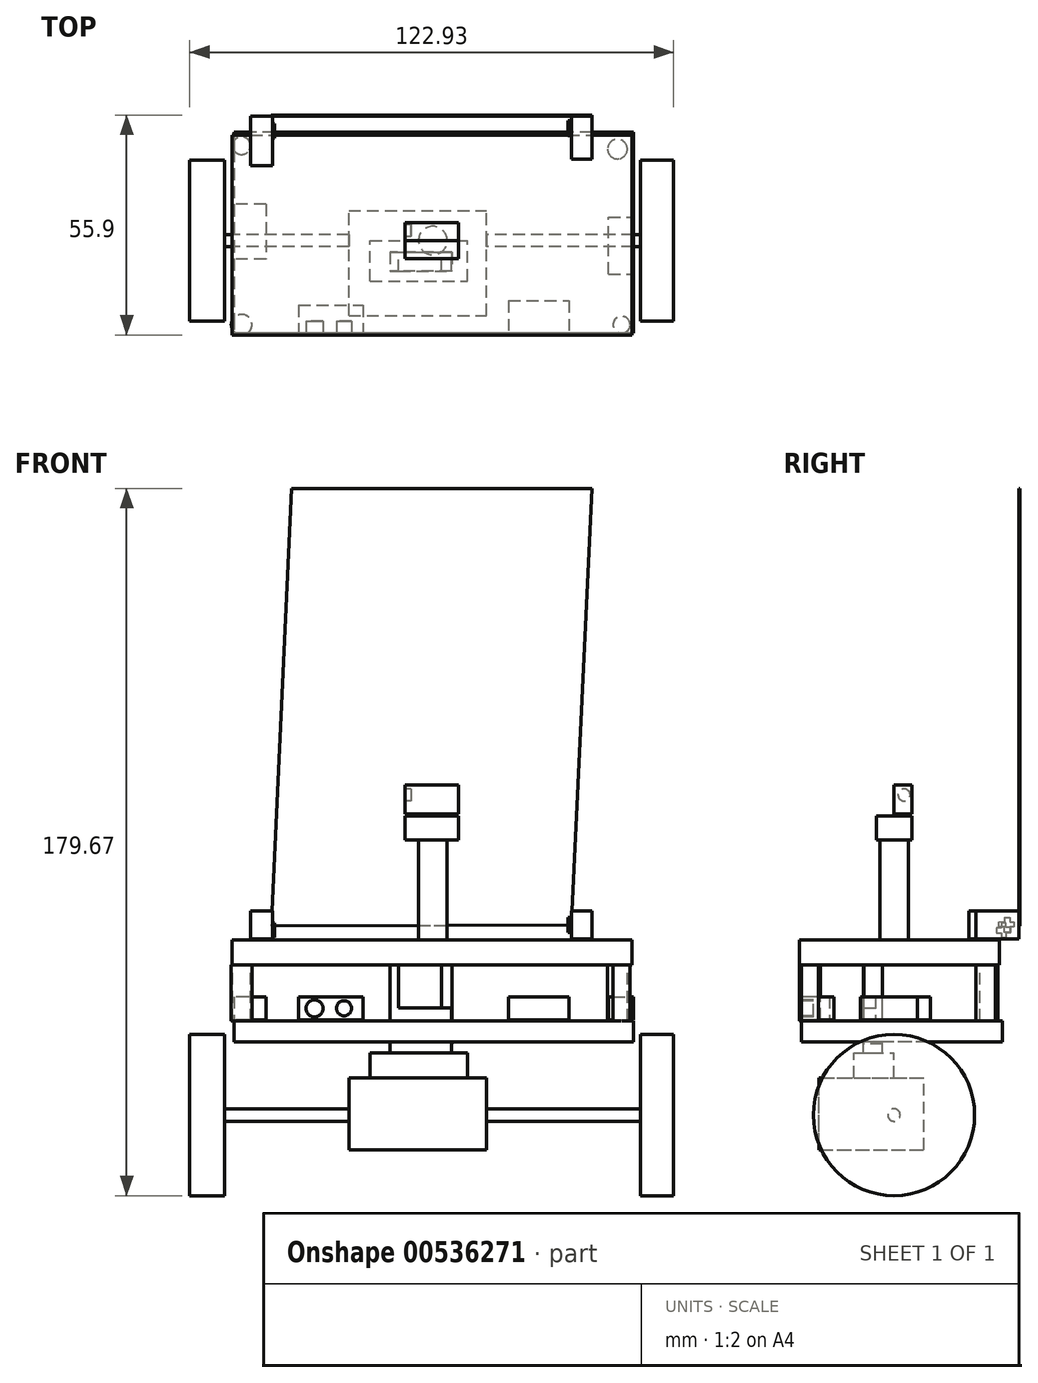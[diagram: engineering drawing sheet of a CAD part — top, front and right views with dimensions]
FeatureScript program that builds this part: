
annotation { "Feature Type Name" : "Feature", "Feature Type Description" : "" }
export const myFeature = defineFeature(function(context is Context, id is Id, definition is map)
    precondition{}
    {
        {
            var Q0;
            Q0=qCreatedBy(makeId("Top.planeOp"),FACE);
            var sketch = newSketch(context, id + "F0", { "sketchPlane" : qUnion([Q0])});
            skLineSegment(sketch, "E0.bottom", {"start": v(-50.99, 26.82) * mm, "end": v(50.61, 26.82) * mm});
            skLineSegment(sketch, "E0.top", {"start": v(-50.99, -23.98) * mm, "end": v(50.61, -23.98) * mm});
            skLineSegment(sketch, "E0.left", {"start": v(-50.99, 26.82) * mm, "end": v(-50.99, -23.98) * mm});
            skLineSegment(sketch, "E0.right", {"start": v(50.61, 26.82) * mm, "end": v(50.61, -23.98) * mm});
            skSolve(sketch);
        }
        {
            var Q0;
            Q0=makeQuery(id+"F0.imprint","IMPRINT",FACE,{"disambiguationData":[TD([[makeQuery(id+"F0.imprint","IMPRINT",EDGE,{"derivedFrom":sQuery(id+"F0.wireOp",EDGE,"E0.bottom")}),-1.0]])]});
            extrude(context, id + "F1", {"entities" : qUnion([Q0]), "depth" : 6.35 * mm, "offsetDistance" : 25.4 * mm});
        }
        {
            var Q0;
            Q0=makeQuery(id+"F1.opExtrude","CAP_FACE",FACE,{"disambiguationData":[OSD([sQuery(id+"F0.wireOp",EDGE,"E0.bottom"),sQuery(id+"F0.wireOp",EDGE,"E0.top"),sQuery(id+"F0.wireOp",EDGE,"E0.left"),sQuery(id+"F0.wireOp",EDGE,"E0.right")])],"isStart":false});
            var sketch = newSketch(context, id + "F2", { "sketchPlane" : qUnion([Q0])});
            skCircle(sketch, "E1", {"center": v(0, 0) * mm, "radius": 3.64 * mm});
            skSolve(sketch);
        }
        {
            var Q0;
            Q0 = qSketchRegion(id + "F2", true);
            extrude(context, id + "F3", {"entities" : qUnion([Q0]), "operationType" : NewBodyOperationType.ADD, "depth" : 25.4 * mm, "offsetDistance" : 25.4 * mm, "hasSecondDirection" : true, "secondDirectionOppositeDirection" : true, "secondDirectionDepth" : 1.02 * mm});
        }
        {
            var Q0;
            Q0=makeQuery(id+"F3.opExtrude","CAP_FACE",FACE,{"disambiguationData":[OSD([sQuery(id+"F2.wireOp",EDGE,"E1")])],"isStart":false});
            var sketch = newSketch(context, id + "F4", { "sketchPlane" : qUnion([Q0])});
            skLineSegment(sketch, "E2.bottom", {"start": v(6.54, -4.52) * mm, "end": v(-7.02, -4.52) * mm});
            skLineSegment(sketch, "E2.top", {"start": v(6.54, 4.54) * mm, "end": v(-7.02, 4.54) * mm});
            skLineSegment(sketch, "E2.left", {"start": v(6.54, -4.52) * mm, "end": v(6.54, 4.54) * mm});
            skLineSegment(sketch, "E2.right", {"start": v(-7.02, -4.52) * mm, "end": v(-7.02, 4.54) * mm});
            skSolve(sketch);
        }
        {
            var Q0;
            Q0 = qSketchRegion(id + "F4", true);
            extrude(context, id + "F5", {"entities" : qUnion([Q0]), "operationType" : NewBodyOperationType.ADD, "depth" : 6.1 * mm, "offsetDistance" : 25.4 * mm});
        }
        {
            var Q0;
            Q0=makeQuery(id+"F5.opExtrude","CAP_FACE",FACE,{"disambiguationData":[OSD([sQuery(id+"F4.wireOp",EDGE,"E2.bottom"),sQuery(id+"F4.wireOp",EDGE,"E2.top"),sQuery(id+"F4.wireOp",EDGE,"E2.left"),sQuery(id+"F4.wireOp",EDGE,"E2.right")])],"isStart":false});
            var sketch = newSketch(context, id + "F6", { "sketchPlane" : qUnion([Q0])});
            skLineSegment(sketch, "E3.bottom", {"start": v(6.54, 0) * mm, "end": v(-7.02, 0) * mm});
            skLineSegment(sketch, "E3.top", {"start": v(6.54, 4.54) * mm, "end": v(-7.02, 4.54) * mm});
            skLineSegment(sketch, "E3.left", {"start": v(6.54, 0) * mm, "end": v(6.54, 4.54) * mm});
            skLineSegment(sketch, "E3.right", {"start": v(-7.02, 0) * mm, "end": v(-7.02, 4.54) * mm});
            skSolve(sketch);
        }
        {
            var Q0;
            Q0 = qSketchRegion(id + "F6", true);
            extrude(context, id + "F7", {"entities" : qUnion([Q0]), "operationType" : NewBodyOperationType.ADD, "depth" : 7.87 * mm, "offsetDistance" : 25.4 * mm, "hasSecondDirection" : true, "secondDirectionOppositeDirection" : false, "secondDirectionDepth" : 0.5 * mm});
        }
        {
            var Q0;
            Q0=makeQuery(id+"F7.boolean.opBoolean","MERGE",FACE,{"derivedFrom":[makeQuery(id+"F5.opExtrude","SWEPT_FACE",FACE,{"disambiguationData":[OSD([sQuery(id+"F4.wireOp",EDGE,"E2.right")])]}),makeQuery(id+"F7.opExtrude","SWEPT_FACE",FACE,{"disambiguationData":[OSD([sQuery(id+"F6.wireOp",EDGE,"tPaWNqs1-bpPp-KasF-azJ7-oUnZ8tWQEHvT.right")])]})]});
            var sketch = newSketch(context, id + "F8", { "sketchPlane" : qUnion([Q0])});
            skCircle(sketch, "E4", {"center": v(-2.58, 43.15) * mm, "radius": 1.54 * mm});
            skCircle(sketch, "E5", {"center": v(2.34, 42.9) * mm, "radius": 1.59 * mm});
            skSolve(sketch);
        }
        {
            var Q0;
            Q0 = qSketchRegion(id + "F8", true);
            extrude(context, id + "F9", {"entities" : qUnion([Q0]), "operationType" : NewBodyOperationType.REMOVE, "oppositeDirection" : true, "depth" : 1.52 * mm, "offsetDistance" : 25.4 * mm});
        }
        {
            var Q0;
            Q0=makeQuery(id+"F1.opExtrude","CAP_FACE",FACE,{"disambiguationData":[OSD([sQuery(id+"F0.wireOp",EDGE,"E0.bottom"),sQuery(id+"F0.wireOp",EDGE,"E0.top"),sQuery(id+"F0.wireOp",EDGE,"E0.left"),sQuery(id+"F0.wireOp",EDGE,"E0.right")])],"isStart":true});
            var sketch = newSketch(context, id + "F10", { "sketchPlane" : qUnion([Q0])});
            skCircle(sketch, "E6", {"center": v(-48.59, 21.36) * mm, "radius": 2.62 * mm});
            skCircle(sketch, "E7", {"center": v(-48.59, -24.13) * mm, "radius": 2.25 * mm});
            skCircle(sketch, "E8", {"center": v(47.96, 21.36) * mm, "radius": 2.16 * mm});
            skCircle(sketch, "E9", {"center": v(46.9, -23.26) * mm, "radius": 2.5 * mm});
            skSolve(sketch);
        }
        {
            var Q0;
            Q0 = qSketchRegion(id + "F10", true);
            extrude(context, id + "F11", {"entities" : qUnion([Q0]), "operationType" : NewBodyOperationType.ADD, "depth" : 14.22 * mm, "offsetDistance" : 25.4 * mm});
        }
        {
            var Q0;
            Q0=makeQuery(id+"F11.opExtrude","CAP_FACE",FACE,{"disambiguationData":[OSD([sQuery(id+"F10.wireOp",EDGE,"E9")])],"isStart":false});
            var sketch = newSketch(context, id + "F12", { "sketchPlane" : qUnion([Q0])});
            skLineSegment(sketch, "E10.bottom", {"start": v(50.97, -27.6) * mm, "end": v(-50.5, -27.6) * mm});
            skLineSegment(sketch, "E10.top", {"start": v(50.97, 23.52) * mm, "end": v(-50.5, 23.52) * mm});
            skLineSegment(sketch, "E10.left", {"start": v(50.97, -27.6) * mm, "end": v(50.97, 23.52) * mm});
            skLineSegment(sketch, "E10.right", {"start": v(-50.5, -27.6) * mm, "end": v(-50.5, 23.52) * mm});
            skSolve(sketch);
        }
        {
            var Q0;
            Q0 = qSketchRegion(id + "F12", true);
            extrude(context, id + "F13", {"entities" : qUnion([Q0]), "operationType" : NewBodyOperationType.ADD, "depth" : 5.33 * mm, "offsetDistance" : 25.4 * mm});
        }
        {
            var Q0;
            {var subQ0=sQuery(id+"F12.wireOp",EDGE,"E10.left");var subQ1=sQuery(id+"F12.wireOp",EDGE,"E10.top");var subQ2=sQuery(id+"F10.wireOp",EDGE,"E8");var subQ3=sQuery(id+"F10.wireOp",EDGE,"E6");var subQ4=sQuery(id+"F12.wireOp",EDGE,"E10.bottom");var subQ5=sQuery(id+"F10.wireOp",EDGE,"E7");var subQ6=sQuery(id+"F12.wireOp",EDGE,"E10.right");Q0=makeQuery(id+"F13.boolean.opBoolean","SPLIT",FACE,{"disambiguationData":[TD([makeQuery(id+"F11.opExtrude","SWEPT_FACE",FACE,{"disambiguationData":[OSD([subQ3])]}),makeQuery(id+"F11.opExtrude","CAP_FACE",FACE,{"disambiguationData":[OSD([subQ3])],"isStart":false}),makeQuery(id+"F11.opExtrude","SWEPT_FACE",FACE,{"disambiguationData":[OSD([subQ5])]}),makeQuery(id+"F11.opExtrude","CAP_FACE",FACE,{"disambiguationData":[OSD([subQ5])],"isStart":false}),makeQuery(id+"F11.opExtrude","SWEPT_FACE",FACE,{"disambiguationData":[OSD([subQ2])]}),makeQuery(id+"F11.opExtrude","CAP_FACE",FACE,{"disambiguationData":[OSD([subQ2])],"isStart":false}),makeQuery(id+"F11.opExtrude","SWEPT_FACE",FACE,{"disambiguationData":[OSD([sQuery(id+"F10.wireOp",EDGE,"E9")])]}),makeQuery(id+"F13.opExtrude","SWEPT_FACE",FACE,{"disambiguationData":[OSD([subQ4])]}),makeQuery(id+"F13.opExtrude","SWEPT_FACE",FACE,{"disambiguationData":[OSD([subQ1])]}),makeQuery(id+"F13.opExtrude","SWEPT_FACE",FACE,{"disambiguationData":[OSD([subQ0])]}),makeQuery(id+"F13.opExtrude","SWEPT_FACE",FACE,{"disambiguationData":[OSD([subQ6])]})])],"derivedFrom":makeQuery(id+"F13.opExtrude","CAP_FACE",FACE,{"disambiguationData":[OSD([subQ4,subQ1,subQ0,subQ6])],"isStart":true})});}
            var sketch = newSketch(context, id + "F14", { "sketchPlane" : qUnion([Q0])});
            skLineSegment(sketch, "E11.bottom", {"start": v(-42.43, 9.27) * mm, "end": v(-50.5, 9.27) * mm});
            skLineSegment(sketch, "E11.top", {"start": v(-42.43, -4.68) * mm, "end": v(-50.5, -4.68) * mm});
            skLineSegment(sketch, "E11.left", {"start": v(-42.43, 9.27) * mm, "end": v(-42.43, -4.68) * mm});
            skLineSegment(sketch, "E11.right", {"start": v(-50.5, 9.27) * mm, "end": v(-50.5, -4.68) * mm});
            skLineSegment(sketch, "E12.bottom", {"start": v(44.61, -8.52) * mm, "end": v(50.97, -8.52) * mm});
            skLineSegment(sketch, "E12.top", {"start": v(44.61, 5.95) * mm, "end": v(50.97, 5.95) * mm});
            skLineSegment(sketch, "E12.left", {"start": v(44.61, -8.52) * mm, "end": v(44.61, 5.95) * mm});
            skLineSegment(sketch, "E12.right", {"start": v(50.97, -8.52) * mm, "end": v(50.97, 5.95) * mm});
            skLineSegment(sketch, "E13.bottom", {"start": v(-34.12, -16.4) * mm, "end": v(-17.71, -16.4) * mm});
            skLineSegment(sketch, "E13.top", {"start": v(-34.12, -23.52) * mm, "end": v(-17.71, -23.52) * mm});
            skLineSegment(sketch, "E13.left", {"start": v(-34.12, -16.4) * mm, "end": v(-34.12, -23.52) * mm});
            skLineSegment(sketch, "E13.right", {"start": v(-17.71, -16.4) * mm, "end": v(-17.71, -23.52) * mm});
            skLineSegment(sketch, "E14.bottom", {"start": v(19.22, -15.3) * mm, "end": v(34.55, -15.3) * mm});
            skLineSegment(sketch, "E14.top", {"start": v(19.22, -23.52) * mm, "end": v(34.55, -23.52) * mm});
            skLineSegment(sketch, "E14.left", {"start": v(19.22, -15.3) * mm, "end": v(19.22, -23.52) * mm});
            skLineSegment(sketch, "E14.right", {"start": v(34.55, -15.3) * mm, "end": v(34.55, -23.52) * mm});
            skSolve(sketch);
        }
        {
            var Q0;
            Q0 = qSketchRegion(id + "F14", true);
            extrude(context, id + "F15", {"entities" : qUnion([Q0]), "operationType" : NewBodyOperationType.ADD, "depth" : 6.1 * mm, "offsetDistance" : 25.4 * mm, "hasSecondDirection" : true, "secondDirectionOppositeDirection" : false, "secondDirectionDepth" : 0.25 * mm});
        }
        {
            var Q0;
            Q0=makeQuery(id+"F15.opExtrude","SWEPT_FACE",FACE,{"disambiguationData":[OSD([sQuery(id+"F14.wireOp",EDGE,"E13.top")])]});
            var sketch = newSketch(context, id + "F16", { "sketchPlane" : qUnion([Q0])});
            skCircle(sketch, "E15", {"center": v(-30.06, -11.05) * mm, "radius": 2.17 * mm});
            skPoint(sketch, "E15.centerSnap0", {"position": v(-34.12, -11.05) * mm});
            skCircle(sketch, "E16", {"center": v(-22.56, -11.05) * mm, "radius": 1.92 * mm});
            skSolve(sketch);
        }
        {
            var Q0;
            Q0 = qSketchRegion(id + "F16", true);
            extrude(context, id + "F17", {"entities" : qUnion([Q0]), "operationType" : NewBodyOperationType.REMOVE, "oppositeDirection" : true, "depth" : 3.05 * mm, "offsetDistance" : 25.4 * mm});
        }
        {
            var Q0;
            Q0=makeQuery(id+"F1.opExtrude","CAP_FACE",FACE,{"disambiguationData":[OSD([sQuery(id+"F0.wireOp",EDGE,"E0.bottom"),sQuery(id+"F0.wireOp",EDGE,"E0.top"),sQuery(id+"F0.wireOp",EDGE,"E0.left"),sQuery(id+"F0.wireOp",EDGE,"E0.right")])],"isStart":false});
            var sketch = newSketch(context, id + "F18", { "sketchPlane" : qUnion([Q0])});
            skLineSegment(sketch, "E17.bottom", {"start": v(40.38, 20.74) * mm, "end": v(35.19, 20.74) * mm});
            skLineSegment(sketch, "E17.top", {"start": v(40.38, 31.67) * mm, "end": v(35.19, 31.67) * mm});
            skLineSegment(sketch, "E17.left", {"start": v(40.38, 20.74) * mm, "end": v(40.38, 31.67) * mm});
            skLineSegment(sketch, "E17.right", {"start": v(35.19, 20.74) * mm, "end": v(35.19, 31.67) * mm});
            skLineSegment(sketch, "E18.bottom", {"start": v(-46.3, 31.67) * mm, "end": v(-40.75, 31.67) * mm});
            skLineSegment(sketch, "E18.top", {"start": v(-46.3, 19.08) * mm, "end": v(-40.75, 19.08) * mm});
            skLineSegment(sketch, "E18.left", {"start": v(-46.3, 31.67) * mm, "end": v(-46.3, 19.08) * mm});
            skLineSegment(sketch, "E18.right", {"start": v(-40.75, 31.67) * mm, "end": v(-40.75, 19.08) * mm});
            skSolve(sketch);
        }
        {
            var Q0;
            Q0 = qSketchRegion(id + "F18", true);
            extrude(context, id + "F19", {"entities" : qUnion([Q0]), "depth" : 7.37 * mm, "offsetDistance" : 25.4 * mm, "hasSecondDirection" : true, "secondDirectionOppositeDirection" : false, "secondDirectionDepth" : 0.25 * mm});
        }
        {
            var Q0;
            Q0=makeQuery(id+"F19.opExtrude","SWEPT_FACE",FACE,{"disambiguationData":[OSD([sQuery(id+"F18.wireOp",EDGE,"E17.right")])]});
            var sketch = newSketch(context, id + "F20", { "sketchPlane" : qUnion([Q0])});
            skLineSegment(sketch, "E19", {"start": v(-28.01, 12.06) * mm, "end": v(-28.01, 10.99) * mm});
            skLineSegment(sketch, "E20", {"start": v(-28.01, 10.99) * mm, "end": v(-28.01, 12.06) * mm});
            skLineSegment(sketch, "E21", {"start": v(-28.01, 12.06) * mm, "end": v(-29.43, 12.06) * mm});
            skLineSegment(sketch, "E22", {"start": v(-29.43, 12.06) * mm, "end": v(-29.43, 10.93) * mm});
            skLineSegment(sketch, "E23", {"start": v(-29.43, 10.93) * mm, "end": v(-30.5, 10.93) * mm});
            skLineSegment(sketch, "E24", {"start": v(-30.5, 10.93) * mm, "end": v(-30.5, 9.65) * mm});
            skLineSegment(sketch, "E25", {"start": v(-30.5, 9.65) * mm, "end": v(-29.43, 9.65) * mm});
            skLineSegment(sketch, "E26", {"start": v(-29.43, 9.65) * mm, "end": v(-29.43, 8.2) * mm});
            skLineSegment(sketch, "E27", {"start": v(-29.43, 8.2) * mm, "end": v(-28.01, 8.2) * mm});
            skLineSegment(sketch, "E28", {"start": v(-28.01, 8.2) * mm, "end": v(-28.01, 9.65) * mm});
            skLineSegment(sketch, "E29", {"start": v(-28.01, 9.65) * mm, "end": v(-26.67, 9.65) * mm});
            skLineSegment(sketch, "E30", {"start": v(-26.67, 9.65) * mm, "end": v(-26.67, 10.93) * mm});
            skLineSegment(sketch, "E31", {"start": v(-26.67, 10.93) * mm, "end": v(-28.01, 10.99) * mm});
            skSolve(sketch);
        }
        {
            var Q0;
            Q0 = qSketchRegion(id + "F20", true);
            extrude(context, id + "F21", {"entities" : qUnion([Q0]), "operationType" : NewBodyOperationType.ADD, "depth" : 0.91 * mm, "offsetDistance" : 25.4 * mm});
        }
        {
            var Q0;
            Q0=makeQuery(id+"F19.opExtrude","SWEPT_FACE",FACE,{"disambiguationData":[OSD([sQuery(id+"F18.wireOp",EDGE,"E18.left")])]});
            var sketch = newSketch(context, id + "F22", { "sketchPlane" : qUnion([Q0])});
            skLineSegment(sketch, "E32", {"start": v(-27.28, 9.38) * mm, "end": v(-27.28, 10.67) * mm});
            skLineSegment(sketch, "E33", {"start": v(-27.28, 10.67) * mm, "end": v(-28.48, 10.67) * mm});
            skLineSegment(sketch, "E34", {"start": v(-28.48, 10.67) * mm, "end": v(-28.48, 9.48) * mm});
            skLineSegment(sketch, "E35", {"start": v(-28.48, 9.48) * mm, "end": v(-29.7, 9.48) * mm});
            skLineSegment(sketch, "E36", {"start": v(-29.7, 9.48) * mm, "end": v(-29.7, 8.21) * mm});
            skLineSegment(sketch, "E37", {"start": v(-29.7, 8.21) * mm, "end": v(-28.55, 8.21) * mm});
            skLineSegment(sketch, "E38", {"start": v(-28.55, 8.21) * mm, "end": v(-28.55, 7.03) * mm});
            skLineSegment(sketch, "E39", {"start": v(-28.55, 7.03) * mm, "end": v(-27.3, 7.03) * mm});
            skLineSegment(sketch, "E40", {"start": v(-27.3, 7.03) * mm, "end": v(-27.3, 8.11) * mm});
            skLineSegment(sketch, "E41", {"start": v(-27.3, 8.11) * mm, "end": v(-26.03, 8.11) * mm});
            skLineSegment(sketch, "E42", {"start": v(-26.03, 8.11) * mm, "end": v(-26.03, 9.34) * mm});
            skLineSegment(sketch, "E43", {"start": v(-26.03, 9.34) * mm, "end": v(-27.28, 9.38) * mm});
            skSolve(sketch);
        }
        {
            var Q0;
            Q0 = qSketchRegion(id + "F22", true);
            extrude(context, id + "F23", {"entities" : qUnion([Q0]), "operationType" : NewBodyOperationType.ADD, "oppositeDirection" : true, "depth" : 6.1 * mm, "offsetDistance" : 25.4 * mm});
        }
        {
            var Q0;
            Q0=makeQuery(id+"F13.opExtrude","CAP_FACE",FACE,{"disambiguationData":[OSD([sQuery(id+"F12.wireOp",EDGE,"E10.bottom"),sQuery(id+"F12.wireOp",EDGE,"E10.top"),sQuery(id+"F12.wireOp",EDGE,"E10.left"),sQuery(id+"F12.wireOp",EDGE,"E10.right")])],"isStart":false});
            var sketch = newSketch(context, id + "F24", { "sketchPlane" : qUnion([Q0])});
            skLineSegment(sketch, "E44.bottom", {"start": v(-10.93, 7.78) * mm, "end": v(-8.7, 7.78) * mm});
            skLineSegment(sketch, "E44.top", {"start": v(-10.93, 2.96) * mm, "end": v(-8.7, 2.96) * mm});
            skLineSegment(sketch, "E44.left", {"start": v(-10.93, 7.78) * mm, "end": v(-10.93, 2.96) * mm});
            skLineSegment(sketch, "E44.right", {"start": v(-8.7, 7.78) * mm, "end": v(-8.7, 2.96) * mm});
            skLineSegment(sketch, "E45.bottom", {"start": v(2.22, 7.6) * mm, "end": v(4.82, 7.6) * mm});
            skLineSegment(sketch, "E45.top", {"start": v(2.22, 2.96) * mm, "end": v(4.82, 2.96) * mm});
            skLineSegment(sketch, "E45.left", {"start": v(2.22, 7.6) * mm, "end": v(2.22, 2.96) * mm});
            skLineSegment(sketch, "E45.right", {"start": v(4.82, 7.6) * mm, "end": v(4.82, 2.96) * mm});
            skSolve(sketch);
        }
        {
            var Q0;
            Q0 = qSketchRegion(id + "F24", true);
            extrude(context, id + "F25", {"entities" : qUnion([Q0]), "operationType" : NewBodyOperationType.ADD, "depth" : 0.5 * mm, "offsetDistance" : 25.4 * mm, "hasSecondDirection" : true, "secondDirectionOppositeDirection" : true, "secondDirectionDepth" : 20.07 * mm});
        }
        {
            var Q0;
            Q0=makeQuery(id+"F25.opExtrude","CAP_FACE",FACE,{"disambiguationData":[OSD([sQuery(id+"F24.wireOp",EDGE,"E44.bottom"),sQuery(id+"F24.wireOp",EDGE,"E44.top"),sQuery(id+"F24.wireOp",EDGE,"E44.left"),sQuery(id+"F24.wireOp",EDGE,"E44.right")])],"isStart":false});
            var sketch = newSketch(context, id + "F26", { "sketchPlane" : qUnion([Q0])});
            skLineSegment(sketch, "E46.bottom", {"start": v(-10.93, 7.78) * mm, "end": v(4.73, 7.78) * mm});
            skLineSegment(sketch, "E46.top", {"start": v(-10.93, 2.96) * mm, "end": v(4.73, 2.96) * mm});
            skLineSegment(sketch, "E46.left", {"start": v(-10.93, 7.78) * mm, "end": v(-10.93, 2.96) * mm});
            skLineSegment(sketch, "E46.right", {"start": v(4.73, 7.78) * mm, "end": v(4.73, 2.96) * mm});
            skSolve(sketch);
        }
        {
            var Q0;
            Q0 = qSketchRegion(id + "F26", true);
            extrude(context, id + "F27", {"entities" : qUnion([Q0]), "operationType" : NewBodyOperationType.ADD, "depth" : 2.3 * mm, "offsetDistance" : 25.4 * mm, "hasSecondDirection" : true, "secondDirectionOppositeDirection" : true, "secondDirectionDepth" : 9.14 * mm});
        }
        {
            var Q0;
            Q0=makeQuery(id+"F27.opExtrude","CAP_FACE",FACE,{"disambiguationData":[OSD([sQuery(id+"F26.wireOp",EDGE,"E46.bottom"),sQuery(id+"F26.wireOp",EDGE,"E46.top"),sQuery(id+"F26.wireOp",EDGE,"E46.left"),sQuery(id+"F26.wireOp",EDGE,"E46.right")])],"isStart":false});
            var sketch = newSketch(context, id + "F28", { "sketchPlane" : qUnion([Q0])});
            skPoint(sketch, "E47.firstSnap0", {"position": v(-10.93, 5.37) * mm});
            skLineSegment(sketch, "E48.bottom", {"start": v(-15.92, 10.23) * mm, "end": v(8.83, 10.23) * mm});
            skLineSegment(sketch, "E48.top", {"start": v(-15.92, 0) * mm, "end": v(8.83, 0) * mm});
            skLineSegment(sketch, "E48.left", {"start": v(-15.92, 10.23) * mm, "end": v(-15.92, 0) * mm});
            skLineSegment(sketch, "E48.right", {"start": v(8.83, 10.23) * mm, "end": v(8.83, 0) * mm});
            skSolve(sketch);
        }
        {
            var Q0;
            Q0 = qSketchRegion(id + "F28", true);
            extrude(context, id + "F29", {"entities" : qUnion([Q0]), "operationType" : NewBodyOperationType.ADD, "depth" : 6.35 * mm, "offsetDistance" : 25.4 * mm});
        }
        {
            var Q0;
            Q0=makeQuery(id+"F29.opExtrude","CAP_FACE",FACE,{"disambiguationData":[OSD([sQuery(id+"F28.wireOp",EDGE,"E48.bottom"),sQuery(id+"F28.wireOp",EDGE,"E48.top"),sQuery(id+"F28.wireOp",EDGE,"E48.left"),sQuery(id+"F28.wireOp",EDGE,"E48.right")])],"isStart":false});
            var sketch = newSketch(context, id + "F30", { "sketchPlane" : qUnion([Q0])});
            skLineSegment(sketch, "E49.bottom", {"start": v(-21.34, 19.05) * mm, "end": v(13.69, 19.05) * mm});
            skLineSegment(sketch, "E49.top", {"start": v(-21.34, -7.6) * mm, "end": v(13.69, -7.6) * mm});
            skLineSegment(sketch, "E49.left", {"start": v(-21.34, 19.05) * mm, "end": v(-21.34, -7.6) * mm});
            skLineSegment(sketch, "E49.right", {"start": v(13.69, 19.05) * mm, "end": v(13.69, -7.6) * mm});
            skSolve(sketch);
        }
        {
            var Q0;
            Q0 = qSketchRegion(id + "F30", true);
            extrude(context, id + "F31", {"entities" : qUnion([Q0]), "operationType" : NewBodyOperationType.ADD, "depth" : 18.29 * mm, "offsetDistance" : 25.4 * mm});
        }
        {
            var Q0;
            Q0=makeQuery(id+"F31.opExtrude","SWEPT_FACE",FACE,{"disambiguationData":[OSD([sQuery(id+"F30.wireOp",EDGE,"E49.right")])]});
            var sketch = newSketch(context, id + "F32", { "sketchPlane" : qUnion([Q0])});
            skCircle(sketch, "E50", {"center": v(0, -38.15) * mm, "radius": 1.57 * mm});
            skSolve(sketch);
        }
        {
            var Q0;
            Q0 = qSketchRegion(id + "F32", true);
            extrude(context, id + "F33", {"entities" : qUnion([Q0]), "operationType" : NewBodyOperationType.ADD, "depth" : 39.12 * mm, "offsetDistance" : 25.4 * mm, "hasSecondDirection" : true, "secondDirectionOppositeDirection" : true, "secondDirectionDepth" : 66.55 * mm});
        }
        {
            var Q0;
            Q0=makeQuery(id+"F19.opExtrude","SWEPT_FACE",FACE,{"disambiguationData":[OSD([sQuery(id+"F18.wireOp",EDGE,"E17.top")])]});
            var sketch = newSketch(context, id + "F34", { "sketchPlane" : qUnion([Q0])});
            skLineSegment(sketch, "E51", {"start": v(-35.19, 10.16) * mm, "end": v(-40.38, 121.03) * mm});
            skLineSegment(sketch, "E52", {"start": v(-40.38, 121.03) * mm, "end": v(35.84, 121.03) * mm});
            skLineSegment(sketch, "E53", {"start": v(35.84, 121.03) * mm, "end": v(41.04, 9.91) * mm});
            skLineSegment(sketch, "E54", {"start": v(41.04, 9.91) * mm, "end": v(-35.19, 10.16) * mm});
            skSolve(sketch);
        }
        {
            var Q0;
            Q0=makeQuery(id+"F33.opExtrude","CAP_FACE",FACE,{"disambiguationData":[OSD([sQuery(id+"F32.wireOp",EDGE,"E50")])],"isStart":true});
            var sketch = newSketch(context, id + "F35", { "sketchPlane" : qUnion([Q0])});
            skCircle(sketch, "E55", {"center": v(0, -38.15) * mm, "radius": 20.48 * mm});
            skSolve(sketch);
        }
        {
            var Q0;
            Q0 = qSketchRegion(id + "F35", true);
            extrude(context, id + "F36", {"entities" : qUnion([Q0]), "operationType" : NewBodyOperationType.ADD, "depth" : 8.9 * mm, "offsetDistance" : 25.4 * mm});
        }
        {
            var Q0;
            Q0=makeQuery(id+"F33.opExtrude","CAP_FACE",FACE,{"disambiguationData":[OSD([sQuery(id+"F32.wireOp",EDGE,"E50")])],"isStart":false});
            var sketch = newSketch(context, id + "F37", { "sketchPlane" : qUnion([Q0])});
            skCircle(sketch, "E56", {"center": v(0, -38.15) * mm, "radius": 20.48 * mm});
            skSolve(sketch);
        }
        {
            var Q0;
            Q0 = qSketchRegion(id + "F37", true);
            extrude(context, id + "F38", {"entities" : qUnion([Q0]), "operationType" : NewBodyOperationType.ADD, "depth" : 8.38 * mm, "offsetDistance" : 25.4 * mm});
        }
        {
            var Q0;
            Q0 = qSketchRegion(id + "F34", true);
            extrude(context, id + "F39", {"entities" : qUnion([Q0]), "depth" : 0.25 * mm, "offsetDistance" : 25.4 * mm});
        }
    });
